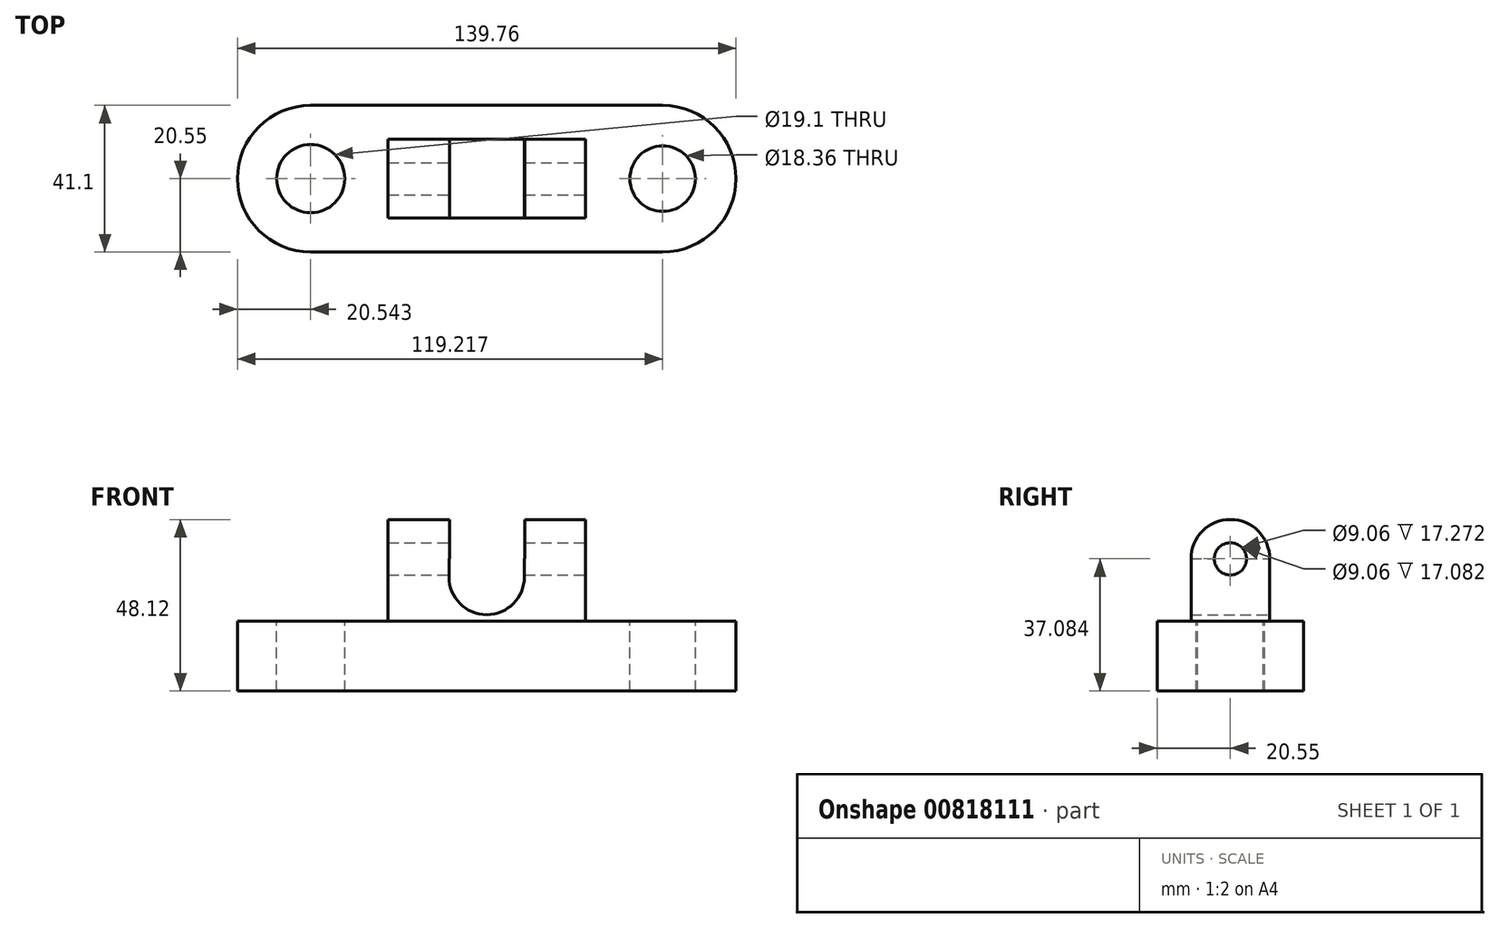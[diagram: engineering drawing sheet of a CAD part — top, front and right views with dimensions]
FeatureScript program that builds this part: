
annotation { "Feature Type Name" : "Feature", "Feature Type Description" : "" }
export const myFeature = defineFeature(function(context is Context, id is Id, definition is map)
    precondition{}
    {
        {
            var Q0;
            Q0=qCreatedBy(makeId("Top.planeOp"),FACE);
            var sketch = newSketch(context, id + "F0", { "sketchPlane" : qUnion([Q0])});
            skLineSegment(sketch, "E0.bottom", {"start": v(49.34, 20.55) * mm, "end": v(-49.34, 20.55) * mm});
            skLineSegment(sketch, "E0.top", {"start": v(49.34, -20.55) * mm, "end": v(-49.34, -20.55) * mm});
            skLineSegment(sketch, "E0.left", {"start": v(49.34, 20.55) * mm, "end": v(49.34, -20.55) * mm});
            skLineSegment(sketch, "E0.right", {"start": v(-49.34, 20.55) * mm, "end": v(-49.34, -20.55) * mm});
            skPoint(sketch, "E0.middle", {"position": v(0, 0) * mm});
            skArc(sketch, "E1", {"start": v(-49.34, 20.55) * mm, "mid": v(-69.88, 0) * mm, "end": v(-49.34, -20.55) * mm});
            skArc(sketch, "E2", {"start": v(49.34, -20.55) * mm, "mid": v(69.88, 0) * mm, "end": v(49.34, 20.55) * mm});
            skSolve(sketch);
        }
        {
            var Q0;
            Q0=qSketchRegion(id+"F0",true);
            var Q1;
            Q1=makeQuery(id+"F0.imprint","IMPRINT",FACE,{"disambiguationData":[TD([[makeQuery(id+"F0.imprint","IMPRINT",EDGE,{"derivedFrom":sQuery(id+"F0.wireOp",EDGE,"E0.bottom")}),1.0]])]});
            extrude(context, id + "F1", {"entities" : qUnion([Q0, Q1]), "depth" : 19.56 * mm, "offsetDistance" : 25.4 * mm});
        }
        {
            var Q0;
            Q0=makeQuery(id+"F1.opExtrude","CAP_FACE",FACE,{"disambiguationData":[OSD([sQuery(id+"F0.wireOp",EDGE,"E0.bottom"),sQuery(id+"F0.wireOp",EDGE,"E0.top"),sQuery(id+"F0.wireOp",EDGE,"E1"),sQuery(id+"F0.wireOp",EDGE,"E2")])],"isStart":false});
            var sketch = newSketch(context, id + "F2", { "sketchPlane" : qUnion([Q0])});
            skCircle(sketch, "E3", {"center": v(-49.34, 0) * mm, "radius": 9.55 * mm});
            skCircle(sketch, "E4", {"center": v(49.34, 0) * mm, "radius": 9.18 * mm});
            skSolve(sketch);
        }
        {
            var Q0;
            Q0=makeQuery(id+"F2.imprint","IMPRINT",FACE,{"disambiguationData":[TD([[makeQuery(id+"F2.imprint","IMPRINT",EDGE,{"derivedFrom":sQuery(id+"F2.wireOp",EDGE,"E4")}),1.0]])]});
            var Q1;
            Q1=makeQuery(id+"F2.imprint","IMPRINT",FACE,{"disambiguationData":[TD([[makeQuery(id+"F2.imprint","IMPRINT",EDGE,{"derivedFrom":sQuery(id+"F2.wireOp",EDGE,"E3")}),1.0]])]});
            extrude(context, id + "F3", {"entities" : qUnion([Q0, Q1]), "operationType" : NewBodyOperationType.REMOVE, "oppositeDirection" : true, "depth" : 38.35 * mm, "offsetDistance" : 25.4 * mm});
        }
        {
            var Q0;
            Q0=makeQuery(id+"F1.opExtrude","CAP_FACE",FACE,{"disambiguationData":[OSD([sQuery(id+"F0.wireOp",EDGE,"E0.bottom"),sQuery(id+"F0.wireOp",EDGE,"E0.top"),sQuery(id+"F0.wireOp",EDGE,"E1"),sQuery(id+"F0.wireOp",EDGE,"E2")])],"isStart":false});
            var sketch = newSketch(context, id + "F4", { "sketchPlane" : qUnion([Q0])});
            skLineSegment(sketch, "E5.bottom", {"start": v(27.66, 11.04) * mm, "end": v(-27.66, 11.04) * mm});
            skLineSegment(sketch, "E5.top", {"start": v(27.66, -11.04) * mm, "end": v(-27.66, -11.04) * mm});
            skLineSegment(sketch, "E5.left", {"start": v(27.66, 11.04) * mm, "end": v(27.66, -11.04) * mm});
            skLineSegment(sketch, "E5.right", {"start": v(-27.66, 11.04) * mm, "end": v(-27.66, -11.04) * mm});
            skPoint(sketch, "E5.middle", {"position": v(0, 0) * mm});
            skSolve(sketch);
        }
        {
            var Q0;
            Q0=qSketchRegion(id+"F4",true);
            var Q1;
            Q1=makeQuery(id+"F4.imprint","IMPRINT",FACE,{"disambiguationData":[TD([[makeQuery(id+"F4.imprint","IMPRINT",EDGE,{"derivedFrom":sQuery(id+"F4.wireOp",EDGE,"E5.bottom")}),1.0]])]});
            extrude(context, id + "F5", {"entities" : qUnion([Q0, Q1]), "operationType" : NewBodyOperationType.ADD, "depth" : 17.53 * mm, "offsetDistance" : 25.4 * mm});
        }
        {
            var Q0;
            Q0=makeQuery(id+"F5.opExtrude","CAP_FACE",FACE,{"disambiguationData":[OSD([sQuery(id+"F4.wireOp",EDGE,"E5.bottom"),sQuery(id+"F4.wireOp",EDGE,"E5.top"),sQuery(id+"F4.wireOp",EDGE,"E5.left"),sQuery(id+"F4.wireOp",EDGE,"E5.right")])],"isStart":false});
            var sketch = newSketch(context, id + "F6", { "sketchPlane" : qUnion([Q0])});
            skLineSegment(sketch, "E6.bottom", {"start": v(-10.57, -11.04) * mm, "end": v(10.57, -11.04) * mm});
            skLineSegment(sketch, "E6.top", {"start": v(-10.57, 11.04) * mm, "end": v(10.57, 11.04) * mm});
            skLineSegment(sketch, "E6.left", {"start": v(-10.57, -11.04) * mm, "end": v(-10.57, 11.04) * mm});
            skLineSegment(sketch, "E6.right", {"start": v(10.57, -11.04) * mm, "end": v(10.57, 11.04) * mm});
            skPoint(sketch, "E6.middle", {"position": v(0, 0) * mm});
            skSolve(sketch);
        }
        {
            var Q0;
            Q0=makeQuery(id+"F6.imprint","IMPRINT",FACE,{"disambiguationData":[TD([[makeQuery(id+"F6.imprint","IMPRINT",EDGE,{"derivedFrom":sQuery(id+"F6.wireOp",EDGE,"E6.bottom")}),-1.0]])]});
            extrude(context, id + "F7", {"entities" : qUnion([Q0]), "operationType" : NewBodyOperationType.REMOVE, "oppositeDirection" : true, "depth" : 5.08 * mm, "offsetDistance" : 25.4 * mm});
        }
        {
            var Q0;
            Q0=makeQuery(id+"F5.opExtrude","SWEPT_FACE",FACE,{"disambiguationData":[OSD([sQuery(id+"F4.wireOp",EDGE,"E5.bottom")])]});
            var sketch = newSketch(context, id + "F8", { "sketchPlane" : qUnion([Q0])});
            skArc(sketch, "E7", {"start": v(-10.57, 32) * mm, "mid": v(0, 21.43) * mm, "end": v(10.57, 32) * mm});
            skSolve(sketch);
        }
        {
            var Q0;
            Q0=qSketchRegion(id+"F8",true);
            var Q1;
            Q1=makeQuery(id+"F8.imprint","IMPRINT",FACE,{"disambiguationData":[TD([[makeQuery(id+"F8.imprint","IMPRINT",EDGE,{"derivedFrom":sQuery(id+"F8.wireOp",EDGE,"E7")}),1.0]])]});
            extrude(context, id + "F9", {"entities" : qUnion([Q0, Q1]), "operationType" : NewBodyOperationType.REMOVE, "oppositeDirection" : true, "depth" : 159.77 * mm, "offsetDistance" : 25.4 * mm});
        }
        {
            var Q0;
            Q0=makeQuery(id+"F5.opExtrude","SWEPT_FACE",FACE,{"disambiguationData":[OSD([sQuery(id+"F4.wireOp",EDGE,"E5.left")])]});
            var sketch = newSketch(context, id + "F10", { "sketchPlane" : qUnion([Q0])});
            skArc(sketch, "E8", {"start": v(11.04, 37.08) * mm, "mid": v(0, 48.12) * mm, "end": v(-11.04, 37.08) * mm});
            skSolve(sketch);
        }
        {
            var Q0;
            Q0=qSketchRegion(id+"F10",true);
            var Q1;
            Q1=makeQuery(id+"F10.imprint","IMPRINT",FACE,{"disambiguationData":[TD([[makeQuery(id+"F10.imprint","IMPRINT",EDGE,{"derivedFrom":sQuery(id+"F10.wireOp",EDGE,"E8")}),1.0]])]});
            extrude(context, id + "F11", {"entities" : qUnion([Q0, Q1]), "operationType" : NewBodyOperationType.ADD, "oppositeDirection" : true, "depth" : 17.02 * mm, "offsetDistance" : 25.4 * mm});
        }
        {
            var Q0;
            Q0=makeQuery(id+"F5.opExtrude","SWEPT_FACE",FACE,{"disambiguationData":[OSD([sQuery(id+"F4.wireOp",EDGE,"E5.right")])]});
            var sketch = newSketch(context, id + "F12", { "sketchPlane" : qUnion([Q0])});
            skArc(sketch, "E9", {"start": v(11.04, 37.08) * mm, "mid": v(0, 48.12) * mm, "end": v(-11.04, 37.08) * mm});
            skSolve(sketch);
        }
        {
            var Q0;
            Q0=qSketchRegion(id+"F12",true);
            var Q1;
            Q1=makeQuery(id+"F12.imprint","IMPRINT",FACE,{"disambiguationData":[TD([[makeQuery(id+"F12.imprint","IMPRINT",EDGE,{"derivedFrom":sQuery(id+"F12.wireOp",EDGE,"E9")}),1.0]])]});
            extrude(context, id + "F13", {"entities" : qUnion([Q0, Q1]), "operationType" : NewBodyOperationType.ADD, "oppositeDirection" : true, "depth" : 17.27 * mm, "offsetDistance" : 25.4 * mm});
        }
        {
            var Q0;
            {var subQ0=sQuery(id+"F4.wireOp",EDGE,"E5.left");Q0=makeQuery(id+"F11.boolean.opBoolean","MERGE",FACE,{"derivedFrom":[makeQuery(id+"F5.opExtrude","SWEPT_FACE",FACE,{"disambiguationData":[OSD([subQ0])]}),makeQuery(id+"F11.opExtrude","CAP_FACE",FACE,{"disambiguationData":[OSD([subQ0,sQuery(id+"F10.wireOp",EDGE,"E8")])],"isStart":true})]});}
            var sketch = newSketch(context, id + "F14", { "sketchPlane" : qUnion([Q0])});
            skCircle(sketch, "E10", {"center": v(0, 37.08) * mm, "radius": 4.53 * mm});
            skSolve(sketch);
        }
        {
            var Q0;
            Q0=makeQuery(id+"F14.imprint","IMPRINT",FACE,{"disambiguationData":[TD([[makeQuery(id+"F14.imprint","IMPRINT",EDGE,{"derivedFrom":sQuery(id+"F14.wireOp",EDGE,"E10")}),1.0]])]});
            extrude(context, id + "F15", {"entities" : qUnion([Q0]), "operationType" : NewBodyOperationType.REMOVE, "oppositeDirection" : true, "depth" : 118.87 * mm, "offsetDistance" : 25.4 * mm});
        }
    });
